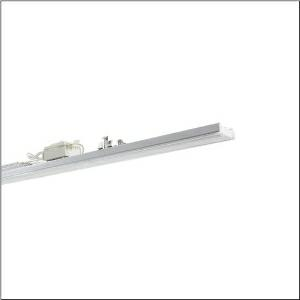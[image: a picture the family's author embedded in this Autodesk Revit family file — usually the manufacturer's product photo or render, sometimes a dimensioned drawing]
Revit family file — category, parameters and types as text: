
# Revit family: licross_21_recessed_ho_52tl1wmn4fxm
name_source: partatom
category: Lighting Fixtures
units: mm (PartAtom-declared; Revit-internal decimal feet)

## family parameters
Cut with Voids When Loaded = No
Host = Face
Light Source = No
Part Type = Normal
Room Calculation Point = No
Round Connector Dimension = Use Diameter
Shared = No

## types (1)
- --- (1 x LED, 15140 lm, 83.1 W, 4000K)
    Apparent Load = 83 VA
    CIE Flux Codes = 73 94 99 100 100
    Color Rendering = 80
    Color Temperature = 4000K
    Default Elevation = 1800 mm
    Description = Licross 21 Recessed HO, luminaire insert, of sheet steel, galvanised, coil coated, white, length: 1.500mm, width: 66mm, height: 67mm, LED rated luminous flux: 15.140lm, light colour: 840, SDCM (Standard Deviation of Colour Matching)MacAdam ≤ 3 SDCM (initial), control gear: ON/OFF Multilumen, with plug, 3-pole, with phase selection, mains connection: 220..240V, AC, 50/60Hz, rated input power: 83W, internal wiring halogen-free, primary optical cover: cover, of PMMA, light emission: direct distribution, primary light characteristic: symmetric, protection rating (complete): IP40, insulation class (complete): insulation class I (protective earthing), certification: CE, ENEC, VDE, UKCA, protection symbol: D if used in an environment without relevant dust loads with corresponding accessories, impact resistance: IK06, permissible ambient temperature for indoor applications: -35..+30°C, corresponds to IFS (International Featured Standards) requirements for safety and quality in the food industry, reducing of maximum allowable ambient temperature of 5°C with ceiling mounting, LABS conformity tested according to VDMA 24364:2018-05, The light source and the operating device comply with the requirements of the Ecodesign Regulation (EU) 2019/2020 and are replaceable in accordance with this regulation, packaging unit: 1 piece
    Height = 58 mm
    Lamp = 1 x LED
    Lamp Light Flux = 15140 lm
    Lamp Power = 83.1 W
    Lamp count = 1
    Length = 1500 mm
    Luminous efficacy = 182 lm/W
    Manufacturer = Siteco
    ModVariant = No
    Model = 52TL1WMN4FXM
    Mounting Place = Ceiling
    Mounting Type = Pendant
    Number of Poles = 1
    OnlyDefault = Yes
    Power Factor = 1
    Product Name = Licross 21 Recessed HO
    Product group = luminaire insert | ceiling pendant
    ProductGroupID = 901
    Protection Class = Protection class I
    Protection Degree = IP 40
    RLX_Detail_Level = 1
    RLX_Emergency_Light_Flux = 0 lm
    RLX_Emergency_Type = 0
    RLX_Emergency_Type_DB = No
    RlxData = <blob elided: 22557 chars, md5=52d26500>
    Socket = socket
    Standby Power = 0 W
    System Light Flux = 15140 lm
    System Power = 83 W
    Type Comments = factory setting: luminous flux: 100 % | (A | C | E) | 195 mA
    Type Image = l_1296930.jpg
    URL = http://relux.com
    VarID = @adj_066595
    Voltage = 0 V
    Weight = 0.00 kg
    Width = 66 mm

## geometry (parser evidence)
native form markers: Blend x4, Sweep x10
no freeform markers — native parametric forms only
